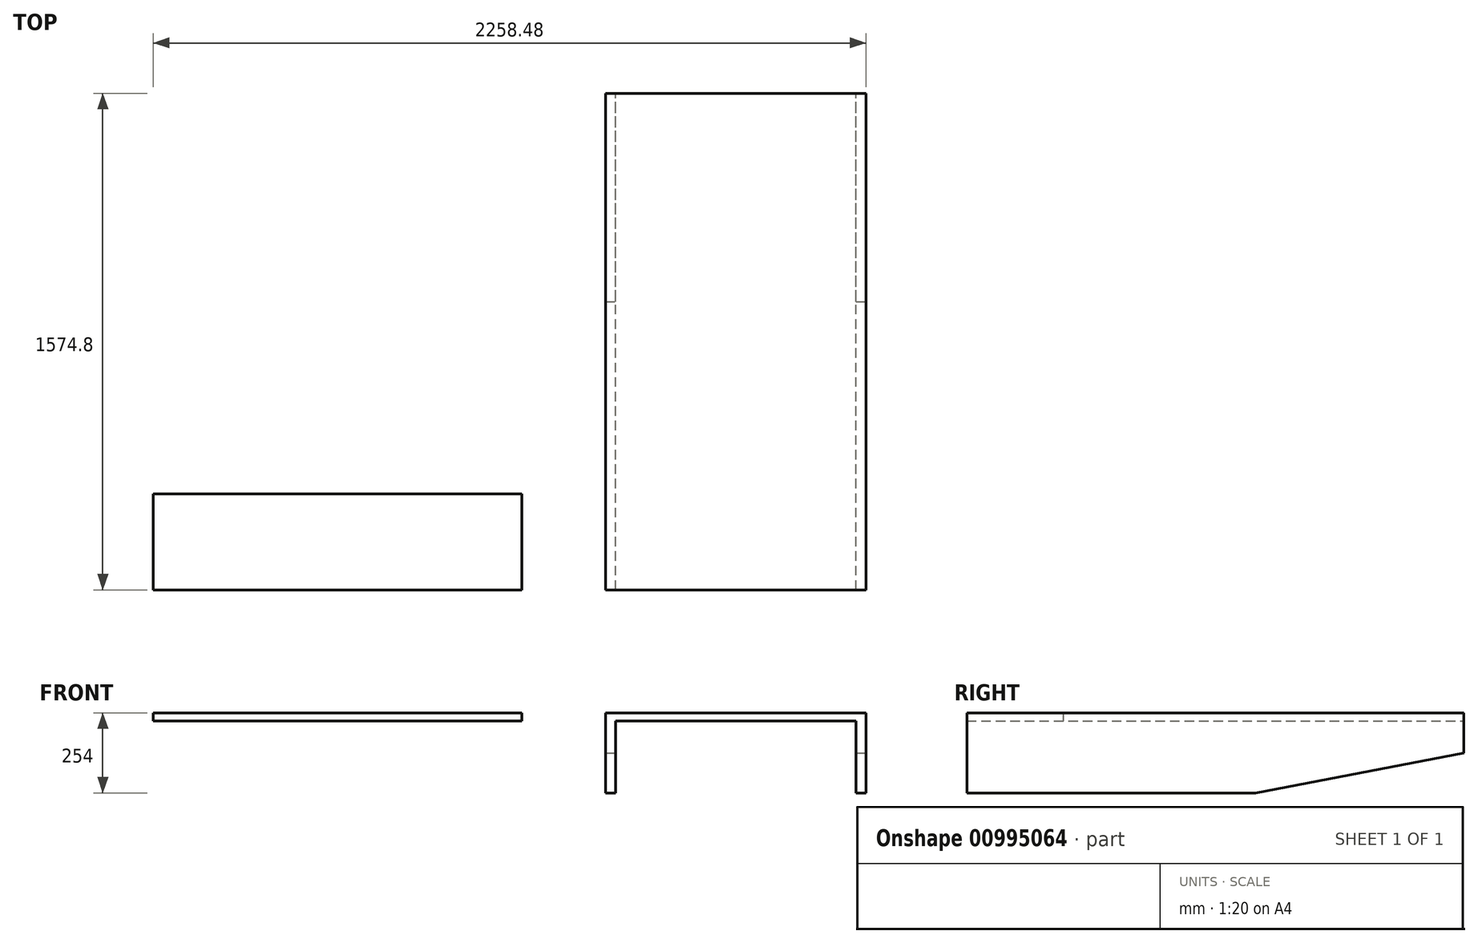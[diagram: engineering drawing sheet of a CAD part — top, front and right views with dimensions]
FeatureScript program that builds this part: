
annotation { "Feature Type Name" : "Feature", "Feature Type Description" : "" }
export const myFeature = defineFeature(function(context is Context, id is Id, definition is map)
    precondition{}
    {
        {
            var Q0;
            Q0=qCreatedBy(makeId("Top.planeOp"),FACE);
            var sketch = newSketch(context, id + "F0", { "sketchPlane" : qUnion([Q0])});
            skLineSegment(sketch, "E0.bottom", {"start": v(0, 0) * mm, "end": v(1168.4, 0) * mm});
            skLineSegment(sketch, "E0.top", {"start": v(0, 1574.8) * mm, "end": v(1168.4, 1574.8) * mm});
            skLineSegment(sketch, "E0.left", {"start": v(0, 0) * mm, "end": v(0, 558.8) * mm});
            skLineSegment(sketch, "E0.right", {"start": v(1168.4, 0) * mm, "end": v(1168.4, 558.8) * mm});
            skLineSegment(sketch, "E1", {"start": v(0, 558.8) * mm, "end": v(120.65, 558.8) * mm});
            skLineSegment(sketch, "E2.bottom", {"start": v(120.65, 558.8) * mm, "end": v(0, 558.8) * mm});
            skLineSegment(sketch, "E2.top", {"start": v(120.65, 863.6) * mm, "end": v(0, 863.6) * mm});
            skLineSegment(sketch, "E2.left", {"start": v(120.65, 558.8) * mm, "end": v(120.65, 863.6) * mm});
            skLineSegment(sketch, "E3.trimOffspring", {"start": v(0, 863.6) * mm, "end": v(0, 1574.8) * mm});
            skLineSegment(sketch, "E4.bottom", {"start": v(1047.75, 558.8) * mm, "end": v(1168.4, 558.8) * mm});
            skLineSegment(sketch, "E4.top", {"start": v(1047.75, 863.6) * mm, "end": v(1168.4, 863.6) * mm});
            skLineSegment(sketch, "E4.left", {"start": v(1047.75, 558.8) * mm, "end": v(1047.75, 863.6) * mm});
            skLineSegment(sketch, "E5.trimOffspring", {"start": v(1168.4, 863.6) * mm, "end": v(1168.4, 1574.8) * mm});
            skLineSegment(sketch, "E6.bottom", {"start": v(171.45, 0) * mm, "end": v(203.2, 0) * mm});
            skLineSegment(sketch, "E6.top", {"start": v(171.45, 1574.8) * mm, "end": v(203.2, 1574.8) * mm});
            skLineSegment(sketch, "E6.left", {"start": v(171.45, 0) * mm, "end": v(171.45, 1574.8) * mm});
            skLineSegment(sketch, "E6.right", {"start": v(203.2, 0) * mm, "end": v(203.2, 1574.8) * mm});
            skLineSegment(sketch, "E7.bottom", {"start": v(996.95, 0) * mm, "end": v(965.2, 0) * mm});
            skLineSegment(sketch, "E7.top", {"start": v(996.95, 1574.8) * mm, "end": v(965.2, 1574.8) * mm});
            skLineSegment(sketch, "E7.left", {"start": v(996.95, 0) * mm, "end": v(996.95, 1574.8) * mm});
            skLineSegment(sketch, "E7.right", {"start": v(965.2, 0) * mm, "end": v(965.2, 1574.8) * mm});
            skLineSegment(sketch, "E8", {"start": v(1066.8, 0) * mm, "end": v(1168.4, 58.66) * mm});
            skLineSegment(sketch, "E9", {"start": v(0, 58.66) * mm, "end": v(101.6, 0) * mm});
            skSolve(sketch);
        }
        {
            var Q0;
            {var subQ0=sQuery(id+"F0.wireOp",EDGE,"E6.right");Q0=makeQuery(id+"F0.imprint","IMPRINT",FACE,{"disambiguationData":[TD([[makeQuery(id+"F0.imprint","IMPRINT",EDGE,{"derivedFrom":subQ0}),-1.0]])]});}
            var Q1;
            {var subQ0=sQuery(id+"F0.wireOp",EDGE,"E7.left");Q1=makeQuery(id+"F0.imprint","IMPRINT",FACE,{"disambiguationData":[TD([[makeQuery(id+"F0.imprint","IMPRINT",EDGE,{"derivedFrom":subQ0}),1.0]])]});}
            var Q2;
            {var subQ0=sQuery(id+"F0.wireOp",EDGE,"E1");Q2=makeQuery(id+"F0.imprint","IMPRINT",FACE,{"disambiguationData":[TD([[makeQuery(id+"F0.imprint","IMPRINT",EDGE,{"derivedFrom":subQ0}),-1.0]])]});}
            var Q3;
            {var subQ2=sQuery(id+"F0.wireOp",EDGE,"E6.left");Q3=makeQuery(id+"F0.imprint","IMPRINT",FACE,{"disambiguationData":[TD([[makeQuery(id+"F0.imprint","IMPRINT",EDGE,{"derivedFrom":subQ2}),-1.0]])]});}
            var Q4;
            {var subQ0=sQuery(id+"F0.wireOp",EDGE,"E4.bottom");Q4=makeQuery(id+"F0.imprint","IMPRINT",FACE,{"disambiguationData":[TD([[makeQuery(id+"F0.imprint","IMPRINT",EDGE,{"derivedFrom":subQ0}),-1.0]])]});}
            extrude(context, id + "F1", {"entities" : qUnion([Q0, Q1, Q2, Q3, Q4]), "depth" : 25.4 * mm, "offsetDistance" : 25.4 * mm});
        }
        {
            var Q0;
            {var subQ2=sQuery(id+"F0.wireOp",EDGE,"E6.left");Q0=makeQuery(id+"F0.imprint","IMPRINT",FACE,{"disambiguationData":[TD([[makeQuery(id+"F0.imprint","IMPRINT",EDGE,{"derivedFrom":subQ2}),-1.0]])]});}
            var Q1;
            {var subQ0=sQuery(id+"F0.wireOp",EDGE,"E7.left");Q1=makeQuery(id+"F0.imprint","IMPRINT",FACE,{"disambiguationData":[TD([[makeQuery(id+"F0.imprint","IMPRINT",EDGE,{"derivedFrom":subQ0}),1.0]])]});}
            extrude(context, id + "F2", {"entities" : qUnion([Q0, Q1]), "operationType" : NewBodyOperationType.ADD, "oppositeDirection" : true, "depth" : 228.6 * mm, "offsetDistance" : 25.4 * mm});
        }
        {
            var Q0;
            Q0=qCreatedBy(makeId("Top.planeOp"),FACE);
            var sketch = newSketch(context, id + "F3", { "sketchPlane" : qUnion([Q0])});
            skLineSegment(sketch, "E10.bottom", {"start": v(-93.13, 0) * mm, "end": v(-1261.53, 0) * mm});
            skLineSegment(sketch, "E10.top", {"start": v(-93.13, 304.8) * mm, "end": v(-1261.53, 304.8) * mm});
            skLineSegment(sketch, "E10.left", {"start": v(-93.13, 0) * mm, "end": v(-93.13, 304.8) * mm});
            skLineSegment(sketch, "E10.right", {"start": v(-1261.53, 0) * mm, "end": v(-1261.53, 304.8) * mm});
            skSolve(sketch);
        }
        {
            var Q0;
            Q0=makeQuery(id+"F3.imprint","IMPRINT",FACE,{"disambiguationData":[TD([[makeQuery(id+"F3.imprint","IMPRINT",EDGE,{"derivedFrom":sQuery(id+"F3.wireOp",EDGE,"E10.bottom")}),-1.0]])]});
            extrude(context, id + "F4", {"entities" : qUnion([Q0]), "depth" : 25.4 * mm, "offsetDistance" : 25.4 * mm});
        }
        {
            var Q0;
            Q0=makeQuery(id+"F2.opExtrude","SWEPT_FACE",FACE,{"disambiguationData":[OSD([sQuery(id+"F0.wireOp",EDGE,"E7.left")])]});
            var sketch = newSketch(context, id + "F5", { "sketchPlane" : qUnion([Q0])});
            skLineSegment(sketch, "E11", {"start": v(914.4, -228.6) * mm, "end": v(1574.8, -101.6) * mm});
            skSolve(sketch);
        }
        {
            var Q0;
            {var subQ0=sQuery(id+"F5.wireOp",EDGE,"E11");Q0=makeQuery(id+"F5.imprint","IMPRINT",FACE,{"disambiguationData":[TD([[makeQuery(id+"F5.imprint","IMPRINT",EDGE,{"derivedFrom":subQ0}),-1.0]])]});}
            extrude(context, id + "F6", {"entities" : qUnion([Q0]), "operationType" : NewBodyOperationType.REMOVE, "oppositeDirection" : true, "depth" : 2540 * mm, "offsetDistance" : 25.4 * mm});
        }
    });
